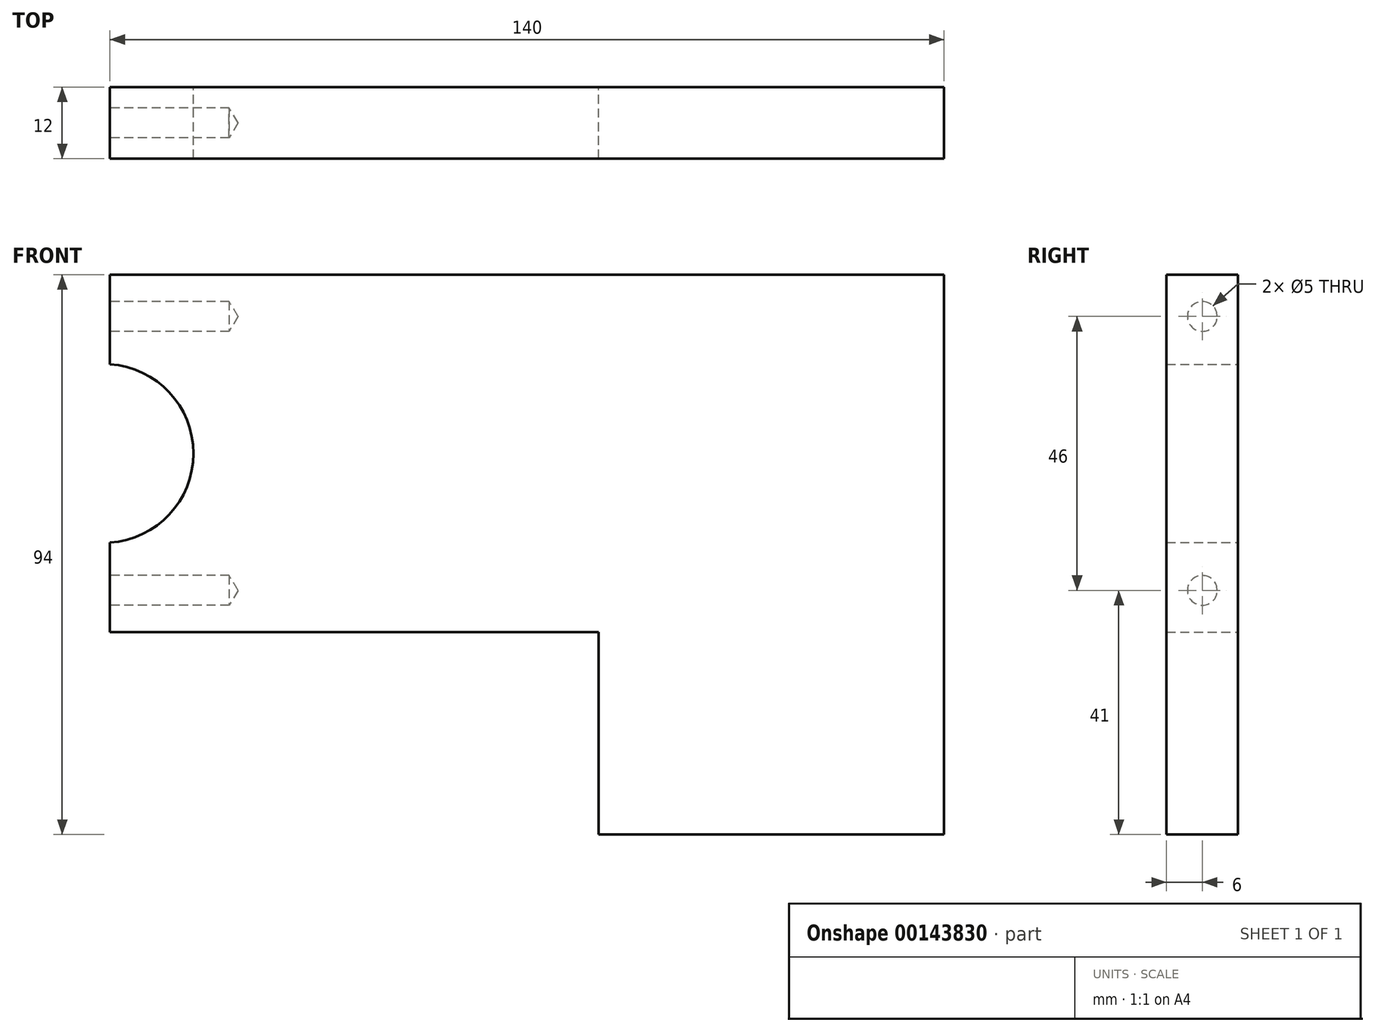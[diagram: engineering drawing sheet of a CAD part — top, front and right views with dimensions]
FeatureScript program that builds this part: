
annotation { "Feature Type Name" : "Feature", "Feature Type Description" : "" }
export const myFeature = defineFeature(function(context is Context, id is Id, definition is map)
    precondition{}
    {
        {
            var Q0;
            Q0=qCreatedBy(makeId("Front.planeOp"),FACE);
            var sketch = newSketch(context, id + "F0", { "sketchPlane" : qUnion([Q0])});
            skLineSegment(sketch, "E0.bottom", {"start": v(70, -47) * mm, "end": v(12, -47) * mm});
            skLineSegment(sketch, "E0.top", {"start": v(70, 47) * mm, "end": v(-70, 47) * mm});
            skLineSegment(sketch, "E0.left", {"start": v(70, -47) * mm, "end": v(70, 47) * mm});
            skLineSegment(sketch, "E0.right", {"start": v(-70, -13) * mm, "end": v(-70, 2.03) * mm});
            skPoint(sketch, "E0.middle", {"position": v(0, 0) * mm});
            skPoint(sketch, "E1.endSnap0", {"position": v(-70, 0) * mm});
            skLineSegment(sketch, "E2", {"start": v(-70, -13) * mm, "end": v(12, -13) * mm});
            skLineSegment(sketch, "E3", {"start": v(12, -47) * mm, "end": v(12, -13) * mm});
            skArc(sketch, "E4", {"start": v(-70, 2.03) * mm, "mid": v(-56, 17) * mm, "end": v(-70, 31.97) * mm});
            skPoint(sketch, "E5.orphan", {"position": v(-70, -47) * mm});
            skLineSegment(sketch, "E6.trimOffspring", {"start": v(-70, 31.97) * mm, "end": v(-70, 47) * mm});
            skSolve(sketch);
        }
        {
            var Q0;
            Q0=makeQuery(id+"F0.imprint","IMPRINT",FACE,{"disambiguationData":[TD([[makeQuery(id+"F0.imprint","IMPRINT",EDGE,{"derivedFrom":sQuery(id+"F0.wireOp",EDGE,"E0.bottom")}),-1.0]])]});
            extrude(context, id + "F1", {"entities" : qUnion([Q0]), "depth" : 12 * mm});
        }
        {
            var Q0;
            Q0=makeQuery(id+"F1.opExtrude","SWEPT_FACE",FACE,{"disambiguationData":[OSD([sQuery(id+"F0.wireOp",EDGE,"E6.trimOffspring")])]});
            var sketch = newSketch(context, id + "F2", { "sketchPlane" : qUnion([Q0])});
            skPoint(sketch, "E7.centerSnap0", {"position": v(12, 39.48) * mm});
            skCircle(sketch, "E8", {"center": v(6, -6) * mm, "radius": 2.5 * mm});
            skPoint(sketch, "E8.centerSnap0", {"position": v(6, 31.97) * mm});
            skCircle(sketch, "E9", {"center": v(6, 40) * mm, "radius": 2.27 * mm});
            skSolve(sketch);
        }
        {
            var Q0;
            Q0=sQuery(id+"F2.wireOp",VERTEX,"E9.center");
            var Q1;
            Q1=sQuery(id+"F2.wireOp",VERTEX,"E8.center");
            var Q2;
            Q2=makeQuery(id+"F1.opExtrude","SWEPT_BODY",BODY,{"disambiguationData":[OSD([sQuery(id+"F0.wireOp",EDGE,"E0.bottom"),sQuery(id+"F0.wireOp",EDGE,"E0.top"),sQuery(id+"F0.wireOp",EDGE,"E0.left"),sQuery(id+"F0.wireOp",EDGE,"E0.right"),sQuery(id+"F0.wireOp",EDGE,"E2"),sQuery(id+"F0.wireOp",EDGE,"E3"),sQuery(id+"F0.wireOp",EDGE,"E4"),sQuery(id+"F0.wireOp",EDGE,"E6.trimOffspring")])]});
            hole(context, id + "F3", {"style" : HoleStyle.SIMPLE, "endStyle" : HoleEndStyle.BLIND, "standardTappedOrClearance" : lookupTablePath({ "standard" : "ISO", "engagement" : "75%", "pitch" : "1 mm", "size" : "M6", "type" : "Tapped" }), "standardBlindInLast" : lookupTablePath({ "standard" : "ISO", "engagement" : "75%", "pitch" : "1 mm", "size" : "M6", "type" : "Tapped" }), "holeDiameter" : 5 * mm, "holeDepth" : 20 * mm, "startFromSketch" : true, "locations" : qUnion([Q0, Q1]), "scope" : qUnion([Q2]), "majorDiameter" : 6 * mm});
        }
    });
